FCSTD DOCUMENT  (FreeCAD 0.19R0.19.2)
Label: motorMount002
License: All rights reserved
LicenseURL: http://en.wikipedia.org/wiki/All_rights_reserved
objects: Sketcher::SketchObject×1
note: 1 computed .brp shape members not serialized (recipe doc carries the construction recipe); baked Part::Feature solids carry a one-line shape summary decoded from their .brp

FEATURE [Sketcher::SketchObject] Sketch
  FullyConstrained = true
  sketch-geometry (9):
    g0: Circle CenterX=0 CenterY=0 CenterZ=0 NormalX=0 NormalY=0 NormalZ=1 AngleXU=0 Radius=2
    g1: Circle CenterX=12.3 CenterY=12.3 CenterZ=0 NormalX=0 NormalY=0 NormalZ=1 AngleXU=0 Radius=2
    g2: Circle CenterX=12.3 CenterY=0 CenterZ=0 NormalX=0 NormalY=0 NormalZ=1 AngleXU=0 Radius=2
    g3: Circle CenterX=0 CenterY=12.3 CenterZ=0 NormalX=0 NormalY=0 NormalZ=1 AngleXU=0 Radius=2
    g4: Circle CenterX=6.15 CenterY=6.15 CenterZ=0 NormalX=0 NormalY=0 NormalZ=1 AngleXU=0 Radius=4.4
    g5: LineSegment StartX=-8.85 StartY=21.15 StartZ=0 EndX=21.15 EndY=21.15 EndZ=0
    g6: LineSegment StartX=21.15 StartY=21.15 StartZ=0 EndX=21.15 EndY=-8.85 EndZ=0
    g7: LineSegment StartX=-8.85 StartY=21.15 StartZ=0 EndX=-8.85 EndY=-8.85 EndZ=0
    g8: LineSegment StartX=-8.85 StartY=-8.85 StartZ=0 EndX=21.15 EndY=-8.85 EndZ=0
  constraints (18):
    c: Block(g0)
    c: Block(g2)
    c: Block(g1)
    c: Block(g3)
    c: Block(g4)
    c: Horizontal(g5)
    c: Distance(g5) = 30
    c: Vertical(g6)
    c: Block(g5)
    c: Distance(g6) = 30
    c: Coincident(g6,g5)
    c: Vertical(g7)
    c: Distance(g7) = 30
    c: Coincident(g7,g5)
    c: Block(g7)
    c: Block(g6)
    c: Coincident(g8,g7)
    c: Coincident(g8,g6)
